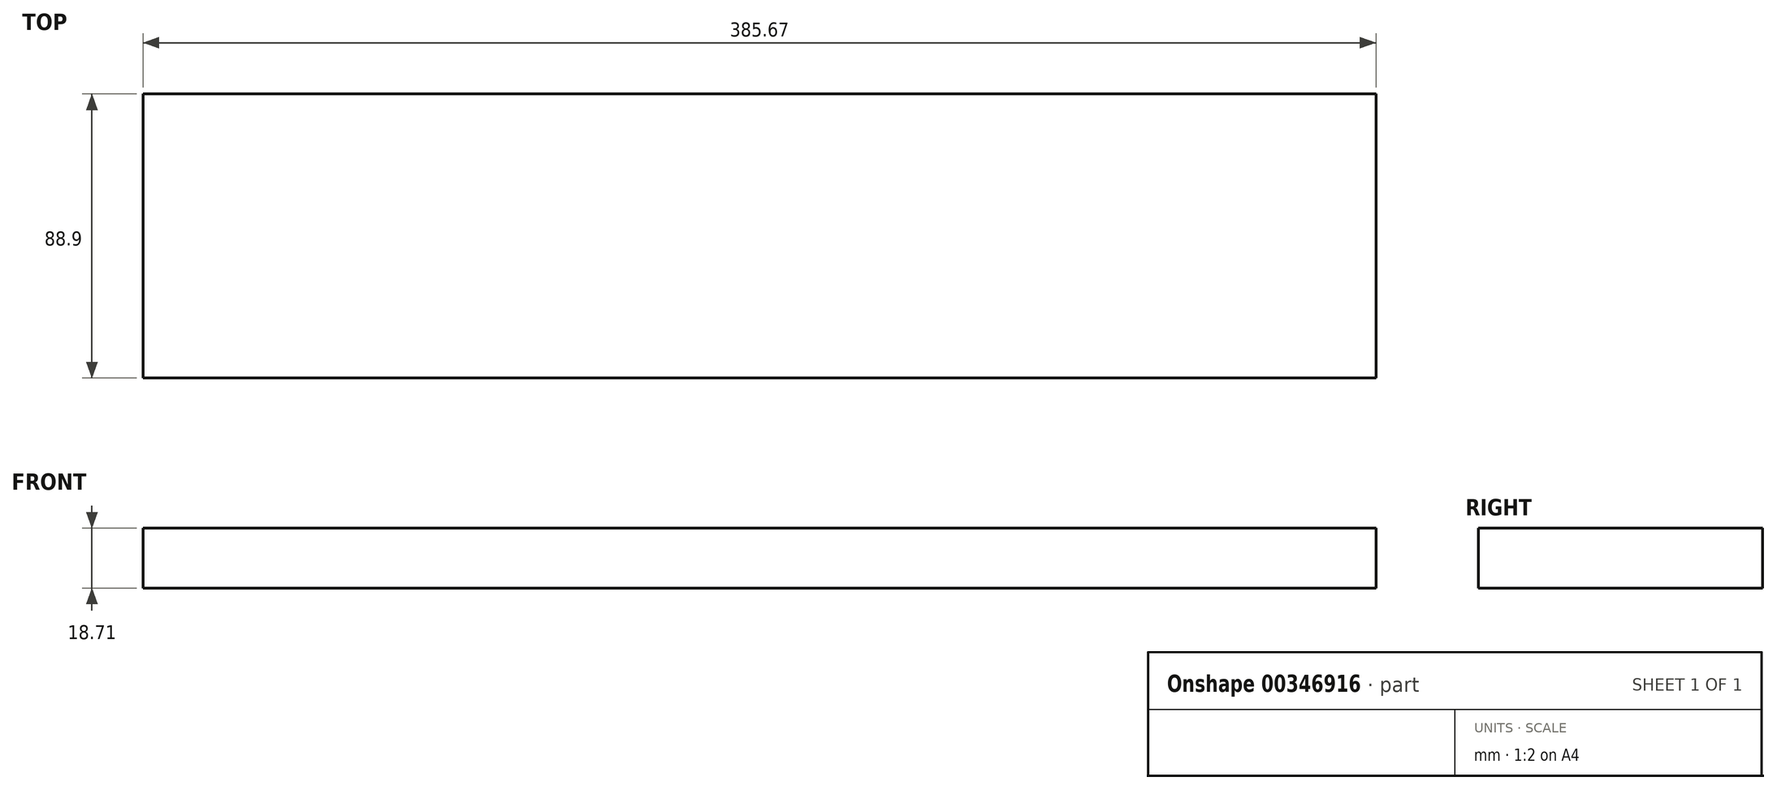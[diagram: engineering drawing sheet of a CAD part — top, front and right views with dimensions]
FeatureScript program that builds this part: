
annotation { "Feature Type Name" : "Feature", "Feature Type Description" : "" }
export const myFeature = defineFeature(function(context is Context, id is Id, definition is map)
    precondition{}
    {
        {
            var Q0;
            Q0=qCreatedBy(makeId("Front.planeOp"),FACE);
            var sketch = newSketch(context, id + "F0", { "sketchPlane" : qUnion([Q0])});
            skLineSegment(sketch, "E0.bottom", {"start": v(-185.28, 28.96) * mm, "end": v(200.39, 28.96) * mm});
            skLineSegment(sketch, "E0.top", {"start": v(-185.28, 10.25) * mm, "end": v(200.39, 10.25) * mm});
            skLineSegment(sketch, "E0.left", {"start": v(-185.28, 28.96) * mm, "end": v(-185.28, 10.25) * mm});
            skLineSegment(sketch, "E0.right", {"start": v(200.39, 28.96) * mm, "end": v(200.39, 10.25) * mm});
            skSolve(sketch);
        }
        {
            var Q0;
            Q0 = qSketchRegion(id + "F0", true);
            extrude(context, id + "F1", {"entities" : qUnion([Q0]), "depth" : 88.9 * mm});
        }
    });
